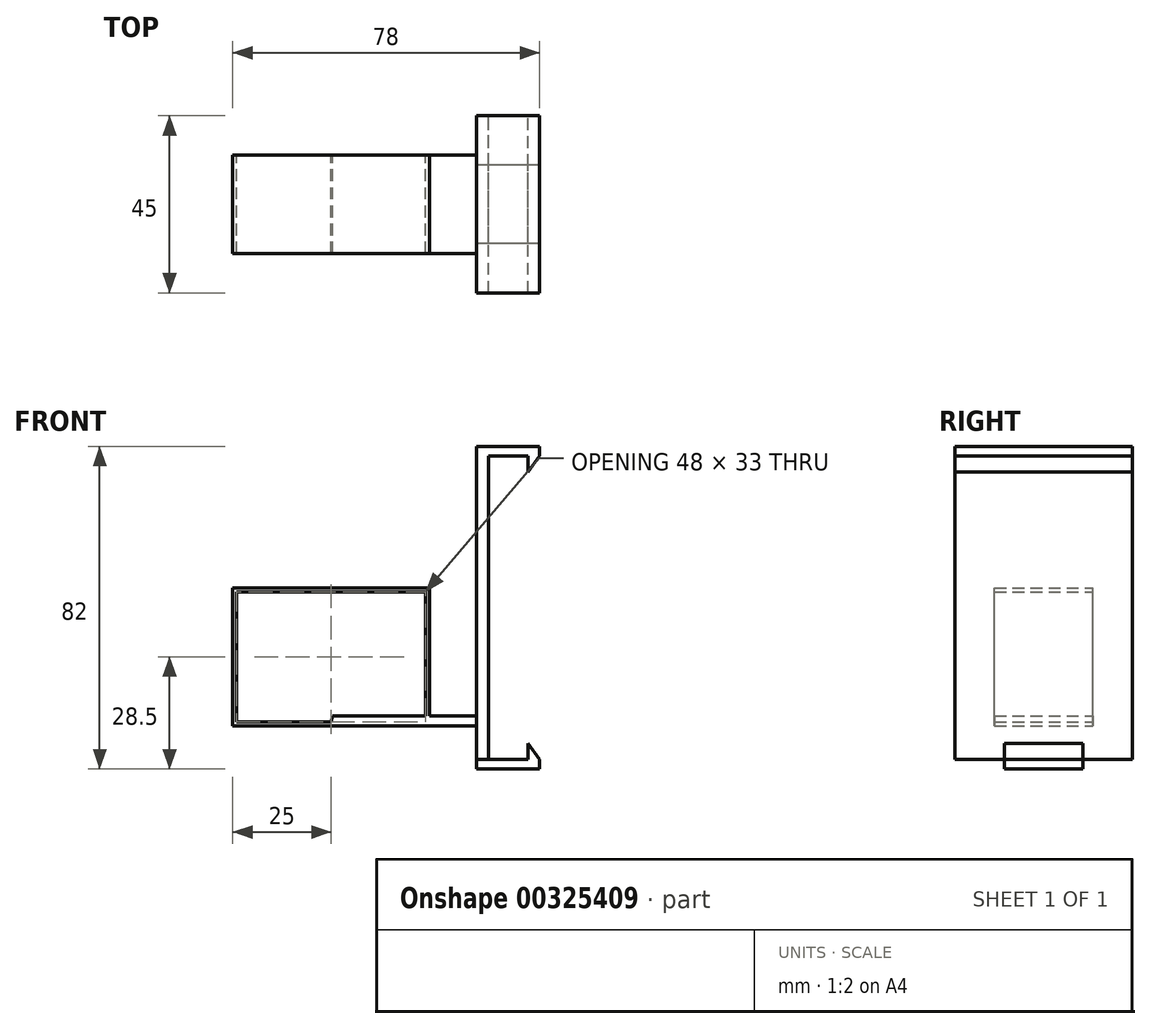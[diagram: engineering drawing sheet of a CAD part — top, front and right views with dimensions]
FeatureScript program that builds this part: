
annotation { "Feature Type Name" : "Feature", "Feature Type Description" : "" }
export const myFeature = defineFeature(function(context is Context, id is Id, definition is map)
    precondition{}
    {
        {
            var Q0;
            Q0=qCreatedBy(makeId("Front.planeOp"),FACE);
            var sketch = newSketch(context, id + "F0", { "sketchPlane" : qUnion([Q0])});
            skLineSegment(sketch, "E0.bottom", {"start": v(-75.5, 75) * mm, "end": v(75.5, 75) * mm});
            skLineSegment(sketch, "E0.top", {"start": v(-75.5, -75) * mm, "end": v(75.5, -75) * mm});
            skLineSegment(sketch, "E0.left", {"start": v(-75.5, 75) * mm, "end": v(-75.5, -75) * mm});
            skLineSegment(sketch, "E0.right", {"start": v(75.5, 75) * mm, "end": v(75.5, -75) * mm});
            skPoint(sketch, "E0.middle", {"position": v(0, 0) * mm});
            skLineSegment(sketch, "E1.bottom", {"start": v(8, 41) * mm, "end": v(-8, 41) * mm});
            skLineSegment(sketch, "E1.top", {"start": v(8, -41) * mm, "end": v(-8, -41) * mm});
            skLineSegment(sketch, "E1.left", {"start": v(8, 41) * mm, "end": v(8, 38.5) * mm});
            skLineSegment(sketch, "E1.right", {"start": v(-8, 41) * mm, "end": v(-8, -41) * mm});
            skLineSegment(sketch, "E2", {"start": v(5, 38.5) * mm, "end": v(-5, 38.5) * mm});
            skLineSegment(sketch, "E3", {"start": v(-5, 38.5) * mm, "end": v(-5, -38.5) * mm});
            skLineSegment(sketch, "E4", {"start": v(-5, -38.5) * mm, "end": v(5, -38.5) * mm});
            skLineSegment(sketch, "E5", {"start": v(8, 38.5) * mm, "end": v(5, 34.5) * mm});
            skLineSegment(sketch, "E6", {"start": v(5, 34.5) * mm, "end": v(5, 38.5) * mm});
            skLineSegment(sketch, "E7", {"start": v(8, -38.5) * mm, "end": v(5, -34.5) * mm});
            skLineSegment(sketch, "E8", {"start": v(5, -34.5) * mm, "end": v(5, -38.5) * mm});
            skLineSegment(sketch, "E9.trimOffspring", {"start": v(8, -38.5) * mm, "end": v(8, -41) * mm});
            skLineSegment(sketch, "E10", {"start": v(-5, -38.5) * mm, "end": v(-8, -38.5) * mm});
            skLineSegment(sketch, "E11.bottom", {"start": v(-8, -30) * mm, "end": v(-44.43, -30) * mm});
            skLineSegment(sketch, "E11.left", {"start": v(-8, -30) * mm, "end": v(-8, 8) * mm});
            skLineSegment(sketch, "E12.bottom", {"start": v(-20, -30) * mm, "end": v(-70, -30) * mm});
            skLineSegment(sketch, "E12.top", {"start": v(-20, 5) * mm, "end": v(-70, 5) * mm});
            skLineSegment(sketch, "E12.left", {"start": v(-20, -30) * mm, "end": v(-20, 5) * mm});
            skLineSegment(sketch, "E12.right", {"start": v(-70, -30) * mm, "end": v(-70, 5) * mm});
            skLineSegment(sketch, "E13.bottom", {"start": v(-21, -29) * mm, "end": v(-69, -29) * mm});
            skLineSegment(sketch, "E13.top", {"start": v(-21, 4) * mm, "end": v(-69, 4) * mm});
            skLineSegment(sketch, "E13.left", {"start": v(-21, -29) * mm, "end": v(-21, 4) * mm});
            skLineSegment(sketch, "E13.right", {"start": v(-69, -29) * mm, "end": v(-69, 4) * mm});
            skLineSegment(sketch, "E14", {"start": v(-21, -27.5) * mm, "end": v(-8, -27.5) * mm});
            skLineSegment(sketch, "E15", {"start": v(-21, -27.5) * mm, "end": v(-44.6, -27.5) * mm});
            skLineSegment(sketch, "E16", {"start": v(-44.6, -27.5) * mm, "end": v(-45, -29) * mm});
            skSolve(sketch);
        }
        {
            var Q0;
            {var subQ1=sQuery(id+"F0.wireOp",EDGE,"E1.bottom");Q0=makeQuery(id+"F0.imprint","IMPRINT",FACE,{"disambiguationData":[TD([[makeQuery(id+"F0.imprint","IMPRINT",EDGE,{"derivedFrom":subQ1}),1.0]])]});}
            extrude(context, id + "F1", {"entities" : qUnion([Q0]), "endBound" : BoundingType.SYMMETRIC, "depth" : 45 * mm});
        }
        {
            var Q0;
            {var subQ1=sQuery(id+"F0.wireOp",EDGE,"E1.top");Q0=makeQuery(id+"F0.imprint","IMPRINT",FACE,{"disambiguationData":[TD([[makeQuery(id+"F0.imprint","IMPRINT",EDGE,{"derivedFrom":subQ1}),-1.0]])]});}
            extrude(context, id + "F2", {"entities" : qUnion([Q0]), "operationType" : NewBodyOperationType.ADD, "endBound" : BoundingType.SYMMETRIC, "depth" : 20 * mm});
        }
        {
            var Q0;
            {var subQ2=sQuery(id+"F0.wireOp",EDGE,"E11.bottom");Q0=makeQuery(id+"F0.imprint","IMPRINT",FACE,{"disambiguationData":[TD([[makeQuery(id+"F0.imprint","IMPRINT",EDGE,{"derivedFrom":subQ2}),-1.0]])]});}
            var Q1;
            {var subQ2=sQuery(id+"F0.wireOp",EDGE,"E11.top");Q1=makeQuery(id+"F0.imprint","IMPRINT",FACE,{"disambiguationData":[TD([[makeQuery(id+"F0.imprint","IMPRINT",EDGE,{"derivedFrom":subQ2}),1.0]])]});}
            extrude(context, id + "F3", {"entities" : qUnion([Q0, Q1]), "operationType" : NewBodyOperationType.ADD, "endBound" : BoundingType.SYMMETRIC, "depth" : 25 * mm});
        }
        {
            var Q0;
            {var subQ6=sQuery(id+"F0.wireOp",EDGE,"E12.top");Q0=makeQuery(id+"F0.imprint","IMPRINT",FACE,{"disambiguationData":[TD([[makeQuery(id+"F0.imprint","IMPRINT",EDGE,{"derivedFrom":subQ6}),1.0]])]});}
            extrude(context, id + "F4", {"entities" : qUnion([Q0]), "operationType" : NewBodyOperationType.ADD, "endBound" : BoundingType.SYMMETRIC, "depth" : 25 * mm});
        }
        {
            var Q0;
            {var subQ4=sQuery(id+"F0.wireOp",EDGE,"E15");Q0=makeQuery(id+"F0.imprint","IMPRINT",FACE,{"disambiguationData":[TD([[makeQuery(id+"F0.imprint","IMPRINT",EDGE,{"derivedFrom":subQ4}),1.0]])]});}
            extrude(context, id + "F5", {"entities" : qUnion([Q0]), "operationType" : NewBodyOperationType.ADD, "endBound" : BoundingType.SYMMETRIC, "depth" : 25 * mm});
        }
    });
